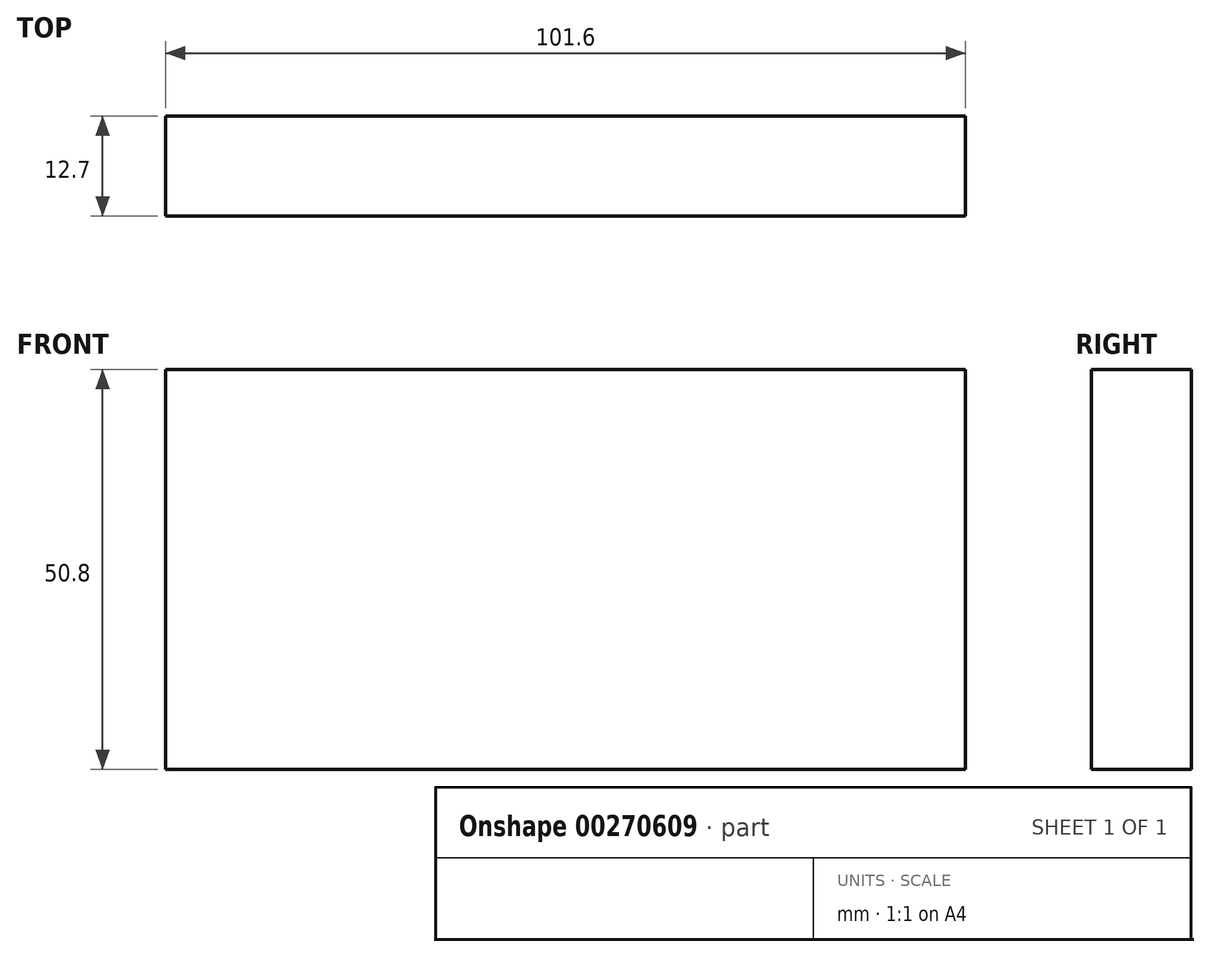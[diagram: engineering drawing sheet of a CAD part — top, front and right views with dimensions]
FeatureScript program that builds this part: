
annotation { "Feature Type Name" : "Feature", "Feature Type Description" : "" }
export const myFeature = defineFeature(function(context is Context, id is Id, definition is map)
    precondition{}
    {
        {
            var Q0;
            Q0=qCreatedBy(makeId("Front.planeOp"),FACE);
            var sketch = newSketch(context, id + "F0", { "sketchPlane" : qUnion([Q0])});
            skLineSegment(sketch, "E0.bottom", {"start": v(50.8, 25.4) * mm, "end": v(-50.8, 25.4) * mm});
            skLineSegment(sketch, "E0.top", {"start": v(50.8, -25.4) * mm, "end": v(-50.8, -25.4) * mm});
            skLineSegment(sketch, "E0.left", {"start": v(50.8, 25.4) * mm, "end": v(50.8, -25.4) * mm});
            skLineSegment(sketch, "E0.right", {"start": v(-50.8, 25.4) * mm, "end": v(-50.8, -25.4) * mm});
            skPoint(sketch, "E0.middle", {"position": v(0, 0) * mm});
            skSolve(sketch);
        }
        {
            var Q0;
            Q0=makeQuery(id+"F0.imprint","IMPRINT",FACE,{"disambiguationData":[TD([[makeQuery(id+"F0.imprint","IMPRINT",EDGE,{"derivedFrom":sQuery(id+"F0.wireOp",EDGE,"E0.bottom")}),1.0]])]});
            extrude(context, id + "F1", {"entities" : qUnion([Q0]), "depth" : 12.7 * mm});
        }
    });
